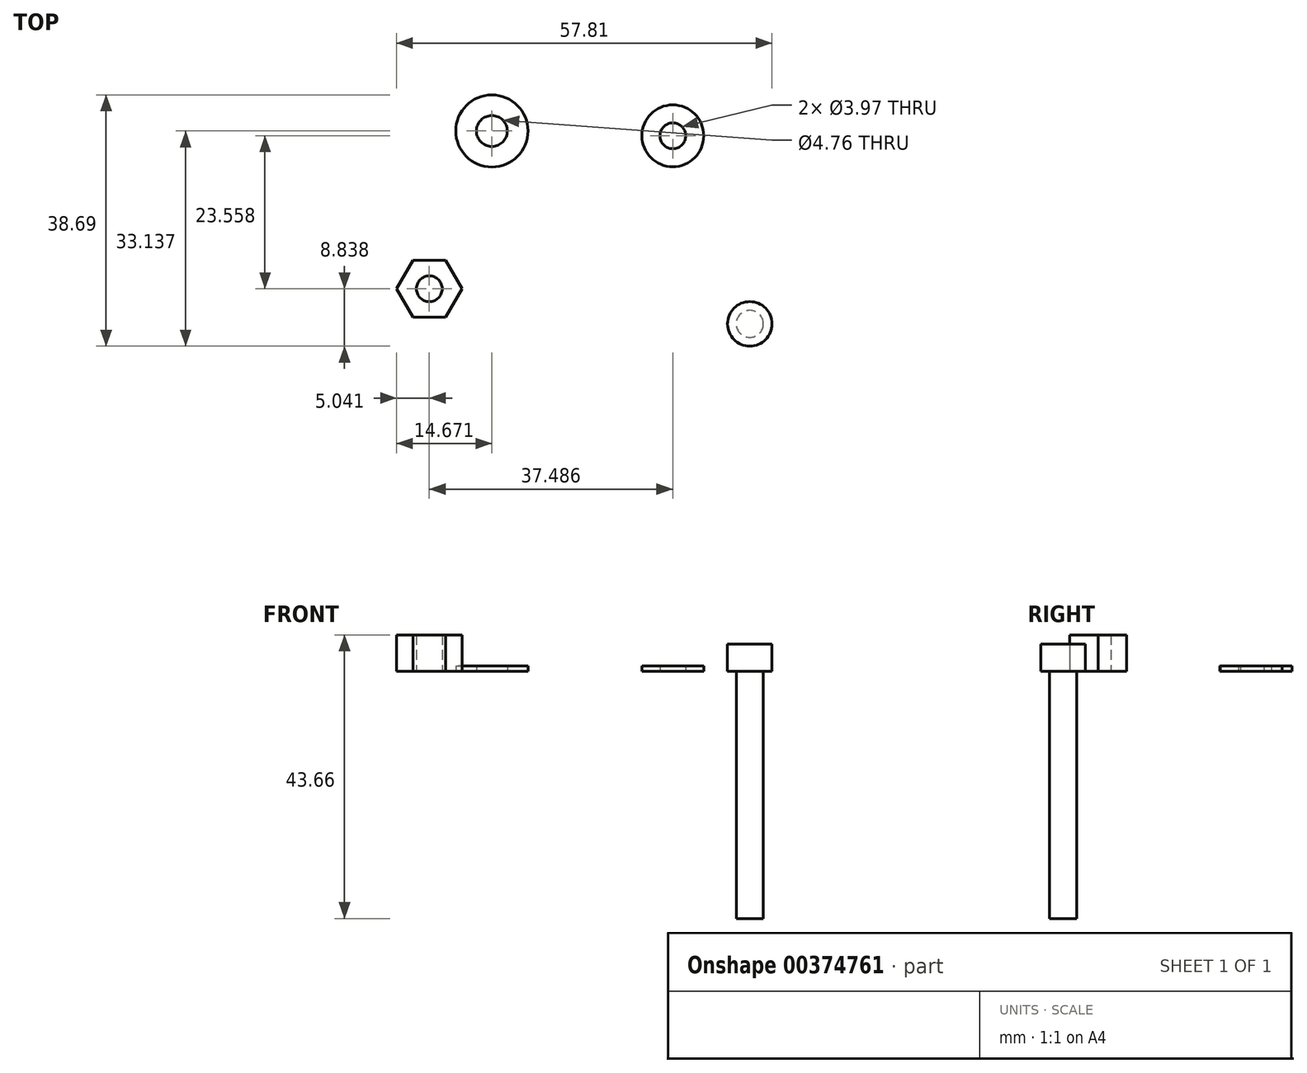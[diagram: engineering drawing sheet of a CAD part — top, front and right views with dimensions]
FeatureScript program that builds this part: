
annotation { "Feature Type Name" : "Feature", "Feature Type Description" : "" }
export const myFeature = defineFeature(function(context is Context, id is Id, definition is map)
    precondition{}
    {
        {
            var Q0;
            Q0=qCreatedBy(makeId("Front.planeOp"),FACE);
            var sketch = newSketch(context, id + "F0", { "sketchPlane" : qUnion([Q0])});
            skLineSegment(sketch, "E0.bottom", {"start": v(0, 0) * mm, "end": v(-3.43, 0) * mm});
            skLineSegment(sketch, "E0.top", {"start": v(0, 4.17) * mm, "end": v(-3.43, 4.17) * mm});
            skLineSegment(sketch, "E0.left", {"start": v(0, 0) * mm, "end": v(0, 4.17) * mm});
            skLineSegment(sketch, "E0.right", {"start": v(-3.43, 0) * mm, "end": v(-3.43, 4.17) * mm});
            skLineSegment(sketch, "E1.bottom", {"start": v(0, 0) * mm, "end": v(-2.08, 0) * mm});
            skLineSegment(sketch, "E1.top", {"start": v(0, -38.1) * mm, "end": v(-2.08, -38.1) * mm});
            skLineSegment(sketch, "E1.left", {"start": v(0, 0) * mm, "end": v(0, -38.1) * mm});
            skLineSegment(sketch, "E1.right", {"start": v(-2.08, 0) * mm, "end": v(-2.08, -38.1) * mm});
            skSolve(sketch);
        }
        {
            var Q0;
            Q0 = qSketchRegion(id + "F0", true);
            var Q1;
            Q1=sQuery(id+"F0.wireOp",EDGE,"E1.left");
            revolve(context, id + "F1", {"entities" : qUnion([Q0]), "axis" : qUnion([Q1]), "revolveType" : RevolveType.FULL});
        }
        {
            var Q0;
            Q0=qCreatedBy(makeId("Top.planeOp"),FACE);
            var sketch = newSketch(context, id + "F2", { "sketchPlane" : qUnion([Q0])});
            skCircle(sketch, "E2", {"center": v(-39.7, 29.7) * mm, "radius": 5.56 * mm});
            skCircle(sketch, "E3", {"center": v(-39.7, 29.7) * mm, "radius": 2.38 * mm});
            skSolve(sketch);
        }
        {
            var Q0;
            Q0 = qSketchRegion(id + "F2", true);
            extrude(context, id + "F3", {"entities" : qUnion([Q0]), "depth" : 0.8 * mm});
        }
        {
            var Q0;
            Q0=qCreatedBy(makeId("Top.planeOp"),FACE);
            var sketch = newSketch(context, id + "F4", { "sketchPlane" : qUnion([Q0])});
            skCircle(sketch, "E4", {"center": v(-11.85, 28.97) * mm, "radius": 4.76 * mm});
            skCircle(sketch, "E5", {"center": v(-11.85, 28.97) * mm, "radius": 1.98 * mm});
            skSolve(sketch);
        }
        {
            var Q0;
            Q0=makeQuery(id+"F4.imprint","IMPRINT",FACE,{"disambiguationData":[TD([[makeQuery(id+"F4.imprint","IMPRINT",EDGE,{"derivedFrom":sQuery(id+"F4.wireOp",EDGE,"E4")}),1.0]])]});
            extrude(context, id + "F5", {"entities" : qUnion([Q0]), "depth" : 0.8 * mm});
        }
        {
            var Q0;
            Q0=qCreatedBy(makeId("Top.planeOp"),FACE);
            var sketch = newSketch(context, id + "F6", { "sketchPlane" : qUnion([Q0])});
            skCircle(sketch, "E6.cCircle", {"center": v(-49.34, 5.4) * mm, "radius": 4.37 * mm, "construction": true});
            skLineSegment(sketch, "E6.0", {"start": v(-51.86, 9.77) * mm, "end": v(-46.82, 9.77) * mm});
            skLineSegment(sketch, "E6.1", {"start": v(-46.82, 9.77) * mm, "end": v(-44.3, 5.4) * mm});
            skLineSegment(sketch, "E6.2", {"start": v(-44.3, 5.4) * mm, "end": v(-46.82, 1.04) * mm});
            skLineSegment(sketch, "E6.3", {"start": v(-46.82, 1.04) * mm, "end": v(-51.86, 1.04) * mm});
            skLineSegment(sketch, "E6.4", {"start": v(-51.86, 1.04) * mm, "end": v(-54.38, 5.4) * mm});
            skLineSegment(sketch, "E6.5", {"start": v(-54.38, 5.4) * mm, "end": v(-51.86, 9.77) * mm});
            skPoint(sketch, "E6.0.midPoint", {"position": v(-49.34, 9.77) * mm});
            skCircle(sketch, "E7", {"center": v(-49.34, 5.4) * mm, "radius": 1.98 * mm});
            skSolve(sketch);
        }
        {
            var Q0;
            Q0 = qSketchRegion(id + "F6", true);
            extrude(context, id + "F7", {"entities" : qUnion([Q0]), "depth" : 5.56 * mm});
        }
    });
